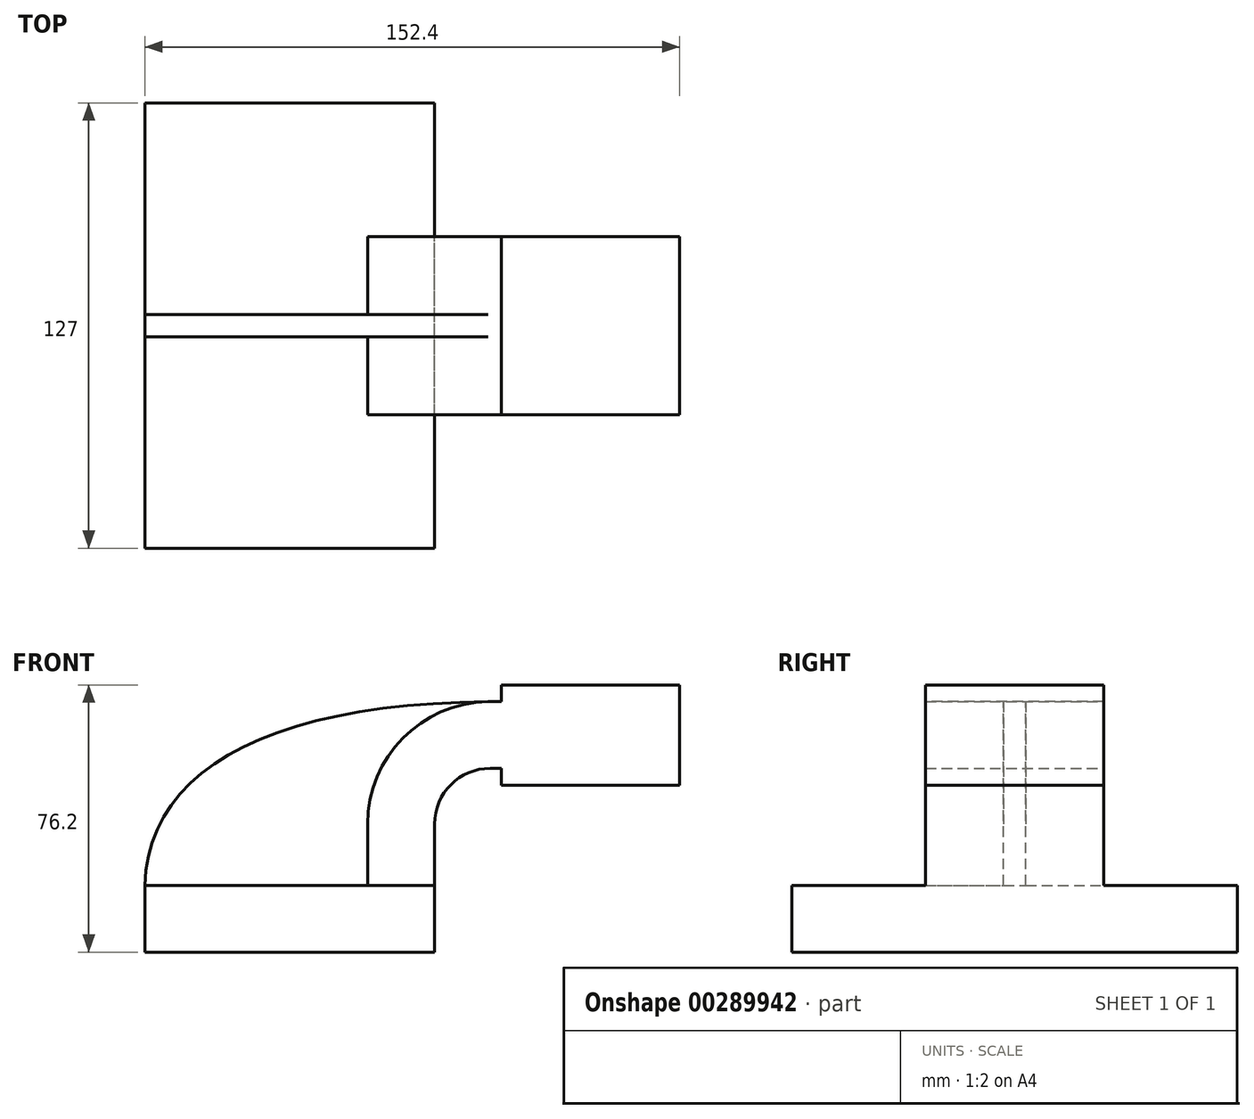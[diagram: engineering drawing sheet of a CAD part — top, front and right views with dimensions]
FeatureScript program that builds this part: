
annotation { "Feature Type Name" : "Feature", "Feature Type Description" : "" }
export const myFeature = defineFeature(function(context is Context, id is Id, definition is map)
    precondition{}
    {
        {
            var Q0;
            Q0=qCreatedBy(makeId("Front.planeOp"),FACE);
            var sketch = newSketch(context, id + "F0", { "sketchPlane" : qUnion([Q0])});
            skLineSegment(sketch, "E0.bottom", {"start": v(41.28, 9.53) * mm, "end": v(-41.28, 9.53) * mm});
            skLineSegment(sketch, "E0.top", {"start": v(41.28, -9.52) * mm, "end": v(-41.28, -9.52) * mm});
            skLineSegment(sketch, "E0.left", {"start": v(41.28, 9.53) * mm, "end": v(41.28, -9.52) * mm});
            skLineSegment(sketch, "E0.right", {"start": v(-41.28, 9.53) * mm, "end": v(-41.28, -9.53) * mm});
            skPoint(sketch, "E0.middle", {"position": v(0, 0) * mm});
            skLineSegment(sketch, "E1.bottom", {"start": v(111.12, 66.68) * mm, "end": v(60.33, 66.68) * mm});
            skLineSegment(sketch, "E1.top", {"start": v(111.12, 38.1) * mm, "end": v(60.33, 38.1) * mm});
            skLineSegment(sketch, "E1.left", {"start": v(111.12, 66.68) * mm, "end": v(111.12, 38.1) * mm});
            skLineSegment(sketch, "E1.right", {"start": v(60.33, 66.68) * mm, "end": v(60.33, 38.1) * mm});
            skPoint(sketch, "E1.middle", {"position": v(85.73, 52.39) * mm});
            skLineSegment(sketch, "E2", {"start": v(41.28, 9.53) * mm, "end": v(41.28, 27) * mm});
            skArc(sketch, "E3", {"start": v(41.28, 27) * mm, "mid": v(45.92, 38.23) * mm, "end": v(57.15, 42.88) * mm});
            skLineSegment(sketch, "E4", {"start": v(57.15, 42.88) * mm, "end": v(85.73, 42.88) * mm});
            skLineSegment(sketch, "E5.0", {"start": v(57.15, 61.93) * mm, "end": v(85.73, 61.93) * mm});
            skArc(sketch, "E5.1", {"start": v(22.23, 27) * mm, "mid": v(32.45, 51.7) * mm, "end": v(57.15, 61.93) * mm});
            skLineSegment(sketch, "E5.2", {"start": v(22.23, 9.53) * mm, "end": v(22.23, 27) * mm});
            skLineSegment(sketch, "E6", {"start": v(85.72, 38.1) * mm, "end": v(85.72, 66.68) * mm});
            skFitSpline(sketch, "E7", {"points": [v(-41.28, 9.52) * mm, v(57.15, 61.93) * mm], "startDerivative": vector(2.86, 99.5) * mm, "endDerivative": vector(188.16, 1.62) * mm});
            skSolve(sketch);
        }
        {
            var Q0;
            Q0=makeQuery(id+"F0.imprint","IMPRINT",FACE,{"disambiguationData":[TD([[makeQuery(id+"F0.imprint","IMPRINT",EDGE,{"derivedFrom":sQuery(id+"F0.wireOp",EDGE,"E0.top")}),-1.0]])]});
            extrude(context, id + "F1", {"entities" : qUnion([Q0]), "endBound" : BoundingType.SYMMETRIC, "depth" : 127 * mm});
        }
        {
            var Q0;
            {var subQ1=sQuery(id+"F0.wireOp",EDGE,"E2");Q0=makeQuery(id+"F0.imprint","IMPRINT",FACE,{"disambiguationData":[TD([[makeQuery(id+"F0.imprint","IMPRINT",EDGE,{"derivedFrom":subQ1}),1.0]])]});}
            var Q1;
            {var subQ0=sQuery(id+"F0.wireOp",EDGE,"E5.0");var subQ1=sQuery(id+"F0.wireOp",EDGE,"E1.right");var subQ2=makeQuery(id+"F0.imprint","INTERSECT",VERTEX,{"derivedFrom":[subQ1,subQ0]});Q1=makeQuery(id+"F0.imprint","IMPRINT",FACE,{"disambiguationData":[TD([[makeQuery(id+"F0.imprint","IMPRINT",EDGE,{"disambiguationData":[TD([[subQ2,-1.0]])],"derivedFrom":subQ1}),1.0]])]});}
            var Q2;
            {var subQ0=sQuery(id+"F0.wireOp",EDGE,"E1.left");Q2=makeQuery(id+"F0.imprint","IMPRINT",FACE,{"disambiguationData":[TD([[makeQuery(id+"F0.imprint","IMPRINT",EDGE,{"derivedFrom":subQ0}),-1.0]])]});}
            var Q3;
            {var subQ0=sQuery(id+"F0.wireOp",EDGE,"E1.right");var subQ1=sQuery(id+"F0.wireOp",EDGE,"E1.bottom");var subQ2=makeQuery(id+"F0.imprint","INTERSECT",VERTEX,{"derivedFrom":[subQ1,subQ0]});Q3=makeQuery(id+"F0.imprint","IMPRINT",FACE,{"disambiguationData":[TD([[makeQuery(id+"F0.imprint","IMPRINT",EDGE,{"disambiguationData":[TD([[subQ2,1.0]])],"derivedFrom":subQ1}),1.0]])]});}
            var Q4;
            {var subQ0=sQuery(id+"F0.wireOp",EDGE,"E1.right");var subQ1=sQuery(id+"F0.wireOp",EDGE,"E1.top");var subQ2=makeQuery(id+"F0.imprint","INTERSECT",VERTEX,{"derivedFrom":[subQ1,subQ0]});Q4=makeQuery(id+"F0.imprint","IMPRINT",FACE,{"disambiguationData":[TD([[makeQuery(id+"F0.imprint","IMPRINT",EDGE,{"disambiguationData":[TD([[subQ2,1.0]])],"derivedFrom":subQ1}),-1.0]])]});}
            extrude(context, id + "F2", {"entities" : qUnion([Q0, Q1, Q2, Q3, Q4]), "operationType" : NewBodyOperationType.ADD, "endBound" : BoundingType.SYMMETRIC, "depth" : 50.8 * mm});
        }
        {
            var Q0;
            {var subQ3=sQuery(id+"F0.wireOp",EDGE,"E5.2");Q0=makeQuery(id+"F0.imprint","IMPRINT",FACE,{"disambiguationData":[TD([[makeQuery(id+"F0.imprint","IMPRINT",EDGE,{"derivedFrom":subQ3}),1.0]])]});}
            extrude(context, id + "F3", {"entities" : qUnion([Q0]), "operationType" : NewBodyOperationType.ADD, "endBound" : BoundingType.SYMMETRIC, "depth" : 6.35 * mm});
        }
    });
